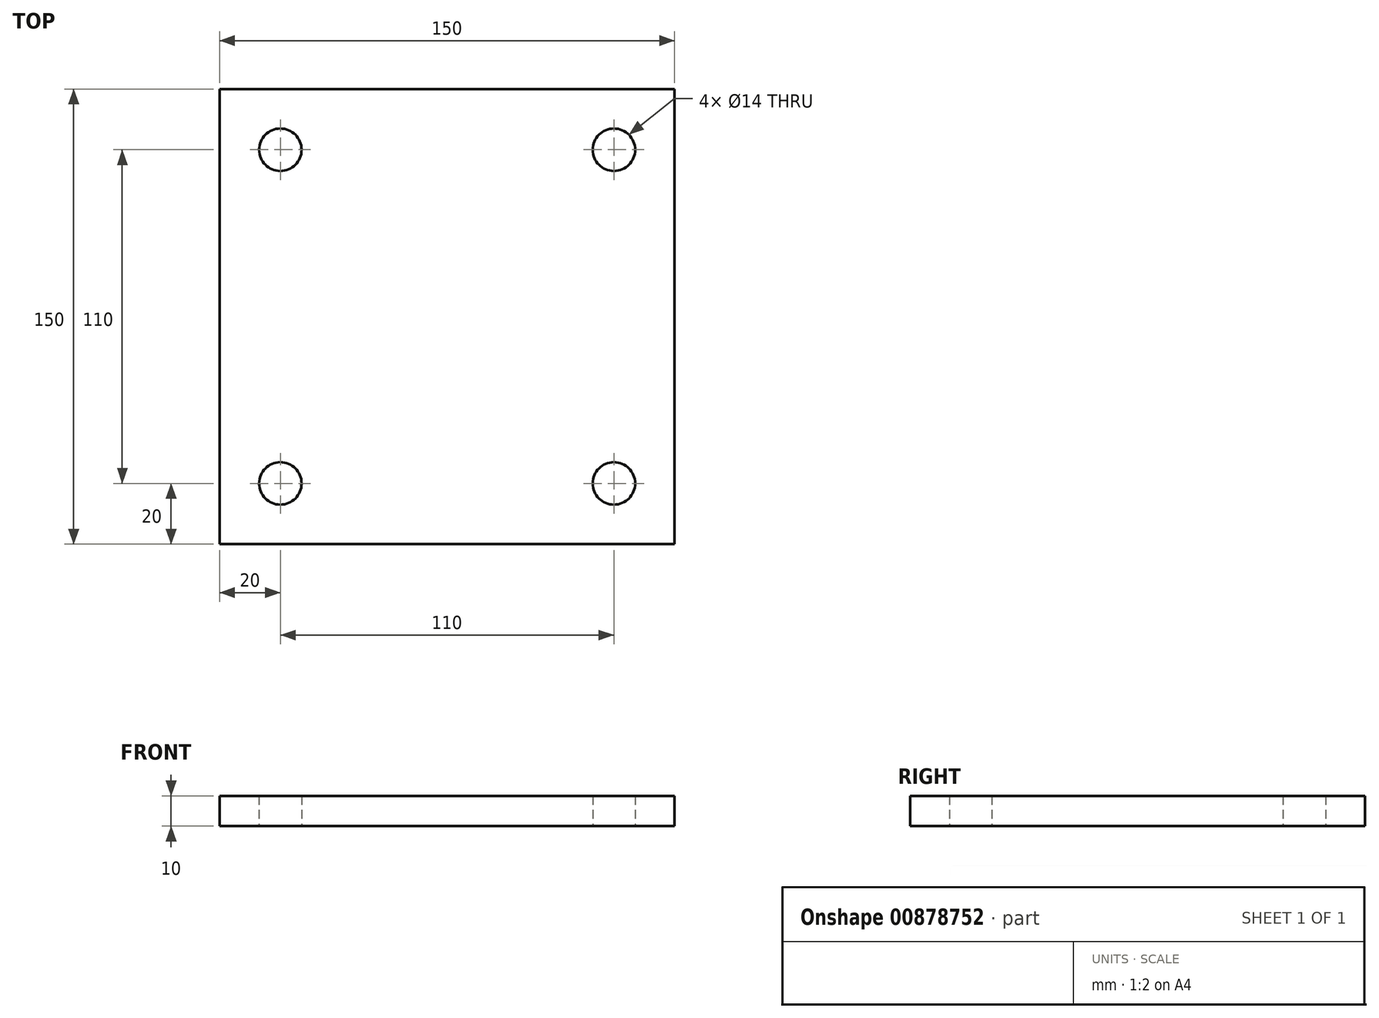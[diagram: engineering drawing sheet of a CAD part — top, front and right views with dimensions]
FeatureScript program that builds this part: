
annotation { "Feature Type Name" : "Feature", "Feature Type Description" : "" }
export const myFeature = defineFeature(function(context is Context, id is Id, definition is map)
    precondition{}
    {
        {
            var Q0;
            Q0=qCreatedBy(makeId("Top.planeOp"),FACE);
            var sketch = newSketch(context, id + "F0", { "sketchPlane" : qUnion([Q0])});
            skLineSegment(sketch, "E0.bottom", {"start": v(75, 75) * mm, "end": v(-75, 75) * mm});
            skLineSegment(sketch, "E0.top", {"start": v(75, -75) * mm, "end": v(-75, -75) * mm});
            skLineSegment(sketch, "E0.left", {"start": v(75, 75) * mm, "end": v(75, -75) * mm});
            skLineSegment(sketch, "E0.right", {"start": v(-75, 75) * mm, "end": v(-75, -75) * mm});
            skPoint(sketch, "E0.middle", {"position": v(0, 0) * mm});
            skCircle(sketch, "E1", {"center": v(55, -55) * mm, "radius": 7 * mm});
            skCircle(sketch, "E2", {"center": v(-55, -55) * mm, "radius": 7 * mm});
            skCircle(sketch, "E3", {"center": v(-55, 55) * mm, "radius": 7 * mm});
            skCircle(sketch, "E4", {"center": v(55, 55) * mm, "radius": 7 * mm});
            skSolve(sketch);
        }
        {
            var Q0;
            Q0=makeQuery(id+"F0.imprint","IMPRINT",FACE,{"disambiguationData":[TD([[makeQuery(id+"F0.imprint","IMPRINT",EDGE,{"derivedFrom":sQuery(id+"F0.wireOp",EDGE,"E0.bottom")}),1.0]])]});
            extrude(context, id + "F1", {"entities" : qUnion([Q0]), "depth" : 10 * mm, "offsetDistance" : 25 * mm});
        }
    });
